# Revit family: 252
name_source: partatom
category: Pipe Accessories
units: mm (PartAtom-declared; Revit-internal decimal feet)

## family parameters
Always vertical = No
Cut with Voids When Loaded = No
Part Type = Normal
Round Connector Dimension = Use Diameter
Shared = Yes
Work Plane-Based = Yes

## types (2) — shared parameters
Default Elevation = 1219 mm
Description = Ball valve, female-female connections with nut and gasket, for pump or mixing valve
H1 = 15 mm
Manufacturer = Giacomini
Series = R252

## per-type parameters (varying)
| type | Height | Nut Dimension | R1 | R2 |
| 1"F x calotta 1-1/2"F | 55 mm | 51 mm | 19 mm  [stored 0.062336 ft] | 23 mm |
| 1-1/4"F x calotta 2"F | 66 mm | 63 mm | 24 mm | 29 mm |

note: column(s) folded — value = type name in every type: Model

note: [stored X ft] marks values corroborated as IEEE doubles in the binary element streams (Revit-internal decimal feet)

## geometry (parser evidence)
native form markers: Sweep x3
no freeform markers — native parametric forms only
